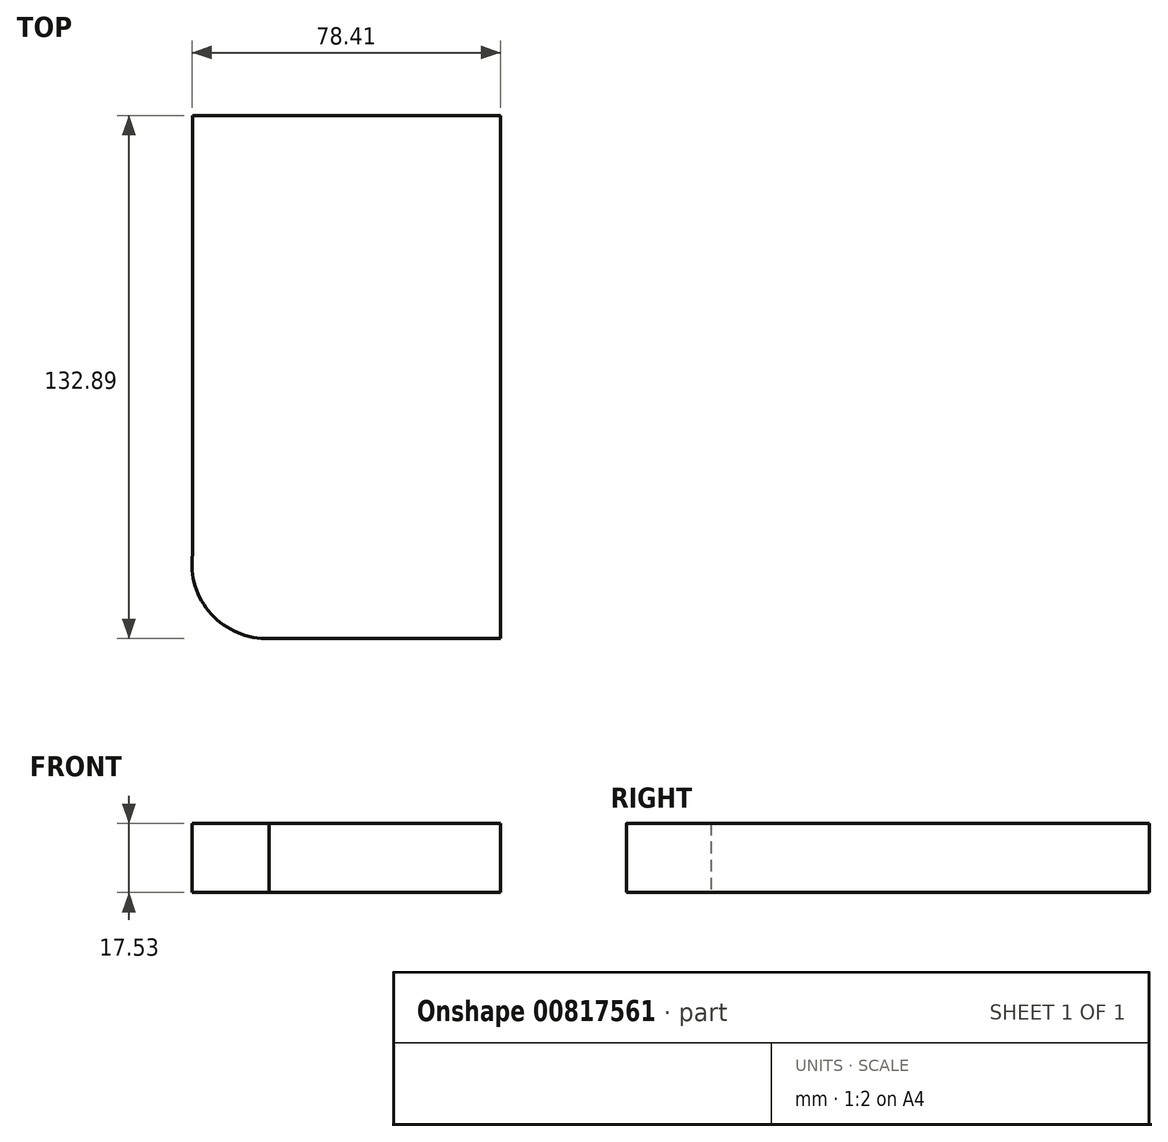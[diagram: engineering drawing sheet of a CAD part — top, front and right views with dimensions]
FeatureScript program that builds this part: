
annotation { "Feature Type Name" : "Feature", "Feature Type Description" : "" }
export const myFeature = defineFeature(function(context is Context, id is Id, definition is map)
    precondition{}
    {
        {
            var Q0;
            Q0=qCreatedBy(makeId("Top.planeOp"),FACE);
            var sketch = newSketch(context, id + "F0", { "sketchPlane" : qUnion([Q0])});
            skLineSegment(sketch, "E0.bottom", {"start": v(-42.4, 61.25) * mm, "end": v(35.85, 61.25) * mm});
            skLineSegment(sketch, "E0.top", {"start": v(-24.3, -71.63) * mm, "end": v(35.85, -71.63) * mm});
            skLineSegment(sketch, "E0.left", {"start": v(-42.4, 61.25) * mm, "end": v(-42.4, -55.15) * mm});
            skLineSegment(sketch, "E0.right", {"start": v(35.85, 61.25) * mm, "end": v(35.85, -71.63) * mm});
            skArc(sketch, "E1", {"start": v(-42.4, -50.23) * mm, "mid": v(-37.62, -65.45) * mm, "end": v(-22.92, -71.63) * mm});
            skSolve(sketch);
        }
        {
            var Q0;
            Q0 = qSketchRegion(id + "F0", true);
            extrude(context, id + "F1", {"entities" : qUnion([Q0]), "depth" : 17.53 * mm, "offsetDistance" : 25.4 * mm});
        }
    });
